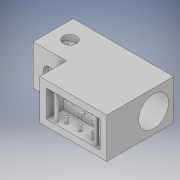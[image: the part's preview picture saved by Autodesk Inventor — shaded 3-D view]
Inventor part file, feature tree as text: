
AUTODESK INVENTOR PART (.ipt)
format: ipt  version: 2018 (Build 220112000, 112)  size: 209,920 bytes
history: native  units: in
note: dims shown in document units (in); Inventor stores cm internally (conversion verified against a paired STEP export)
features: sketch x15, extrude x13
ambient origin geometry x8: Origin, YZ Plane, XZ Plane, XY Plane, X Axis, Y Axis, Z Axis, Center Point
bodies: Solid1 (feature_tree)
feature tree (28):
  extrude  "Extrusion1"  Depth=0.3937in
  extrude  "Extrusion2"  Depth=0.315in
  sketch  "Sketch5"  dims[d5=0.1575in d6=0.0984in d7=0.0in]
  sketch  "Sketch6"  dims[d14=0.0197in d15=0.0197in]
  extrude  "Extrusion4"  Depth=0.0984in TaperAngle=0.0deg
  extrude  "Extrusion5"  Depth=0.0197in
  extrude  "Extrusion12"  Depth=0.1575in TaperAngle=0.0deg
  extrude  "Extrusion13"  Depth=0.2362in
  extrude  "Extrusion14"  Depth=0.1969in TaperAngle=0.0deg
  extrude  "Extrusion15"  Depth=0.5906in TaperAngle=0.0deg
  extrude  "Extrusion16"  Depth=0.0197in TaperAngle=0.0deg
  sketch  "Sketch19"  dims[d52=0.0197in d53=0.0197in]
  extrude  "Extrusion17"  Depth=0.0197in
  extrude  "Extrusion18"  Depth=0.0197in
  extrude  "Extrusion19"  Depth=0.0197in
  sketch  "Sketch23"  dims[d61=0.0197in]
  extrude  "Extrusion20"  Depth=0.0197in
  sketch  "Sketch1"  dims[d0=0.3937in d1=0.2362in]
  sketch  "Sketch2"  dims[d2=0.1575in d3=0.0in d4=0.315in]
  sketch  "Sketch14"  dims[d16=0.1575in d17=0.0in d18=0.1575in d19=0.0in]
  sketch  "Sketch15"  dims[d40=0.2362in d41=0.0in d42=0.2362in]
  sketch  "Sketch16"  dims[d43=0.2362in d44=0.1969in d45=0.0in]
  sketch  "Sketch17"  dims[d46=0.1772in d47=0.5906in d48=0.0in]
  sketch  "Sketch18"  dims[d49=0.0197in d50=0.0197in d51=0.0in]
  sketch  "Sketch20"  dims[d54=0.0197in d55=0.0197in]
  sketch  "Sketch21"  dims[d56=0.0197in d57=0.0197in]
  sketch  "Sketch22"  dims[d58=0.0197in d59=0.0in d60=0.0197in]
  sketch  "Sketch24"  dims[d62=0.0197in d63=0.0315in d64=0.0in d65=0.0197in d66=0.0197in d67=0.0197in d68=0.0315in d69=0.0in d70=0.0787in d71=0.2362in d72=0.0in d73=0.0787in d74=0.2362in d75=0.0in]
